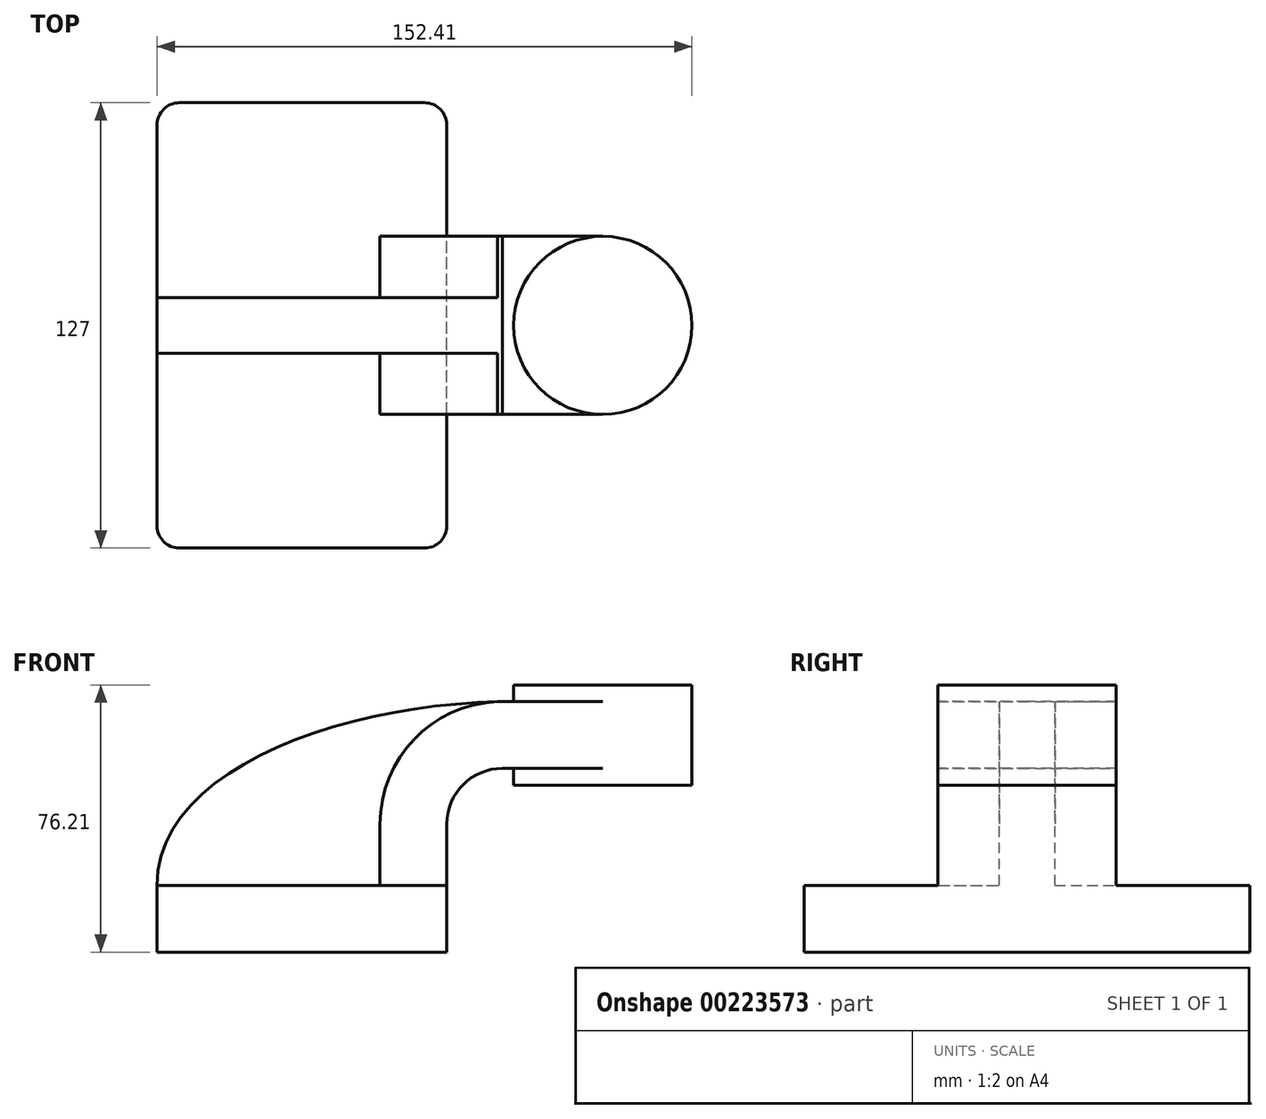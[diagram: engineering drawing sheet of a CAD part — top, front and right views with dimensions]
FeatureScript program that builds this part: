
annotation { "Feature Type Name" : "Feature", "Feature Type Description" : "" }
export const myFeature = defineFeature(function(context is Context, id is Id, definition is map)
    precondition{}
    {
        {
            var Q0;
            Q0=qCreatedBy(makeId("Front.planeOp"),FACE);
            var sketch = newSketch(context, id + "F0", { "sketchPlane" : qUnion([Q0])});
            skLineSegment(sketch, "E0.bottom", {"start": v(41.27, 9.53) * mm, "end": v(-41.28, 9.53) * mm});
            skLineSegment(sketch, "E0.top", {"start": v(41.28, -9.52) * mm, "end": v(-41.27, -9.52) * mm});
            skLineSegment(sketch, "E0.left", {"start": v(41.28, 9.53) * mm, "end": v(41.28, -9.52) * mm});
            skLineSegment(sketch, "E0.right", {"start": v(-41.28, 9.53) * mm, "end": v(-41.27, -9.52) * mm});
            skPoint(sketch, "E0.middle", {"position": v(0, 0) * mm});
            skLineSegment(sketch, "E1.bottom", {"start": v(111.12, 38.1) * mm, "end": v(60.32, 38.1) * mm});
            skLineSegment(sketch, "E1.top", {"start": v(111.12, 66.68) * mm, "end": v(60.32, 66.68) * mm});
            skLineSegment(sketch, "E1.left", {"start": v(111.12, 38.1) * mm, "end": v(111.12, 66.68) * mm});
            skLineSegment(sketch, "E1.right", {"start": v(60.32, 38.1) * mm, "end": v(60.32, 66.68) * mm});
            skPoint(sketch, "E1.middle", {"position": v(85.72, 52.39) * mm});
            skLineSegment(sketch, "E2", {"start": v(41.27, 9.53) * mm, "end": v(41.27, 27) * mm});
            skArc(sketch, "E3", {"start": v(41.27, 27) * mm, "mid": v(45.92, 38.23) * mm, "end": v(57.15, 42.88) * mm});
            skFitSpline(sketch, "E4", {"points": [v(-41.28, 9.53) * mm, v(57.15, 61.93) * mm], "startDerivative": vector(-0.24, 100.29) * mm, "endDerivative": vector(135.27, 2.27) * mm});
            skLineSegment(sketch, "E5", {"start": v(57.15, 42.88) * mm, "end": v(85.72, 42.88) * mm});
            skLineSegment(sketch, "E6", {"start": v(85.72, 38.1) * mm, "end": v(85.72, 66.68) * mm});
            skLineSegment(sketch, "E7.0", {"start": v(57.15, 61.93) * mm, "end": v(85.72, 61.93) * mm});
            skArc(sketch, "E7.1", {"start": v(22.23, 27) * mm, "mid": v(32.45, 51.7) * mm, "end": v(57.15, 61.93) * mm});
            skLineSegment(sketch, "E7.2", {"start": v(22.23, 9.53) * mm, "end": v(22.23, 27) * mm});
            skSolve(sketch);
        }
        {
            var Q0;
            Q0=makeQuery(id+"F0.imprint","IMPRINT",FACE,{"disambiguationData":[TD([[makeQuery(id+"F0.imprint","IMPRINT",EDGE,{"derivedFrom":sQuery(id+"F0.wireOp",EDGE,"E0.top")}),-1.0]])]});
            extrude(context, id + "F1", {"entities" : qUnion([Q0]), "endBound" : BoundingType.SYMMETRIC, "depth" : 127 * mm});
        }
        {
            var Q0;
            {var subQ1=sQuery(id+"F0.wireOp",EDGE,"E2");Q0=makeQuery(id+"F0.imprint","IMPRINT",FACE,{"disambiguationData":[TD([[makeQuery(id+"F0.imprint","IMPRINT",EDGE,{"derivedFrom":subQ1}),1.0]])]});}
            var Q1;
            {var subQ0=sQuery(id+"F0.wireOp",EDGE,"E5");var subQ1=sQuery(id+"F0.wireOp",EDGE,"E1.right");var subQ2=makeQuery(id+"F0.imprint","INTERSECT",VERTEX,{"derivedFrom":[subQ1,subQ0]});Q1=makeQuery(id+"F0.imprint","IMPRINT",FACE,{"disambiguationData":[TD([[makeQuery(id+"F0.imprint","IMPRINT",EDGE,{"disambiguationData":[TD([[subQ2,-1.0]])],"derivedFrom":subQ1}),-1.0]])]});}
            extrude(context, id + "F2", {"entities" : qUnion([Q0, Q1]), "operationType" : NewBodyOperationType.ADD, "endBound" : BoundingType.SYMMETRIC, "depth" : 50.8 * mm});
        }
        {
            var Q0;
            {var subQ3=sQuery(id+"F0.wireOp",EDGE,"E7.2");Q0=makeQuery(id+"F0.imprint","IMPRINT",FACE,{"disambiguationData":[TD([[makeQuery(id+"F0.imprint","IMPRINT",EDGE,{"derivedFrom":subQ3}),1.0]])]});}
            extrude(context, id + "F3", {"entities" : qUnion([Q0]), "operationType" : NewBodyOperationType.ADD, "endBound" : BoundingType.SYMMETRIC, "depth" : 15.88 * mm});
        }
        {
            var Q0;
            {var subQ0=sQuery(id+"F0.wireOp",EDGE,"E1.left");Q0=makeQuery(id+"F0.imprint","IMPRINT",FACE,{"disambiguationData":[TD([[makeQuery(id+"F0.imprint","IMPRINT",EDGE,{"derivedFrom":subQ0}),1.0]])]});}
            var Q1;
            Q1=sQuery(id+"F0.wireOp",EDGE,"E6");
            revolve(context, id + "F4", {"operationType" : NewBodyOperationType.ADD, "entities" : qUnion([Q0]), "axis" : qUnion([Q1]), "revolveType" : RevolveType.FULL});
        }
        {
            var Q0;
            Q0=makeQuery(id+"F1.opExtrude","CAP_EDGE",EDGE,{"disambiguationData":[OSD([sQuery(id+"F0.wireOp",EDGE,"E0.left")])],"isStart":false});
            var Q1;
            Q1=makeQuery(id+"F1.opExtrude","CAP_EDGE",EDGE,{"disambiguationData":[OSD([sQuery(id+"F0.wireOp",EDGE,"E0.right")])],"isStart":false});
            var Q2;
            Q2=makeQuery(id+"F1.opExtrude","CAP_EDGE",EDGE,{"disambiguationData":[OSD([sQuery(id+"F0.wireOp",EDGE,"E0.right")])],"isStart":true});
            var Q3;
            Q3=makeQuery(id+"F1.opExtrude","CAP_EDGE",EDGE,{"disambiguationData":[OSD([sQuery(id+"F0.wireOp",EDGE,"E0.left")])],"isStart":true});
            fillet(context, id + "F5", {"entities" : qUnion([Q0, Q1, Q2, Q3]), "radius" : 6.35 * mm, "tangentPropagation" : true, "allowEdgeOverflow" : false});
        }
    });
